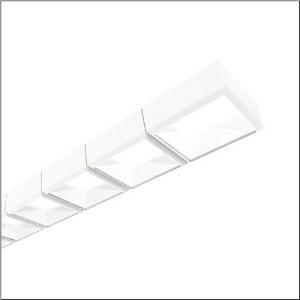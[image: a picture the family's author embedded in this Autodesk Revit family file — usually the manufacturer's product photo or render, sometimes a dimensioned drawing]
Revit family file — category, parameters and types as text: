
# Revit family: scriptus_r__11_5mz314d04wa_e059
name_source: partatom
category: Lighting Fixtures
units: mm (PartAtom-declared; Revit-internal decimal feet)

## family parameters
Cut with Voids When Loaded = No
Host = Face
Light Source = No
Part Type = Normal
Room Calculation Point = No
Round Connector Dimension = Use Diameter
Shared = No

## types (1)
- Scriptus® 11 (1 x LED 4000K / CRI = 80 (unbekannt), 3220 lm / 4820 lm, 4000K)
    Apparent Load = 120 VA
    CIE Flux Codes = - - - 0 100 / 82 95 99 100 100
    Color Rendering = 80
    Color Temperature = 4000K
    Default Elevation = 1800 mm
    Description = Scriptus® 11, office luminaire, primary optical cover: lenses, CAT 2 (L<= 3000cd/m²), light emission: direct/indirect distribution, primary light characteristic: symmetric, installation type: suspended mounting, LED, rated luminous flux: 16.060lm, luminous efficacy: 133lm/W, light colour: 840, colour temperature: 4000K, control gear: DALI, with terminal, 5-pole, mains connection: 230V, AC, 50Hz, rated input power: 120W, LED, control gear: ECG DALI, housing, luminaire housing, of aluminium, traffic white (RAL 9016), length: 3.088mm, width: 114mm, height: 57mm, protection rating (complete): IP20, insulation class (complete): insulation class I (protective earthing), certification: CE, ENEC, VDE, protection symbol: F, permissible operating ambient temperature: 0..+35°C, standard: EN 50419, packaging unit: 1 piece
    Height = 57 mm
    Lamp = 1 x LED 4000K / CRI >= 80 (unbekannt)
    Lamp Light Flux = 3220 lm / 4820 lm
    Lamp count = 1
    Length = 3088 mm
    Luminous efficacy = 134 lm/W
    Manufacturer = Siteco
    ModVariant = No
    Model = 5MZ314D04WA
    Mounting Place = Ceiling
    Mounting Type = Pendant
    Number of Poles = 1
    OnlyDefault = Yes
    Power Factor = 1
    Product Name = Scriptus® 11
    Product group = office luminaire | ceiling pendant
    ProductGroupID = 904
    Protection Class = Protection class I
    Protection Degree = IP 20
    RLX_Detail_Level = 1
    RLX_Emergency_Light_Flux = 0 lm
    RLX_Emergency_Type = 0
    RLX_Emergency_Type_DB = No
    RlxData = <blob elided: 31925 chars, md5=0f39a516>
    Socket = socket
    Standby Power = 0 W
    System Light Flux = 16080 lm
    System Power = 120 W
    Type Comments = Product without accessories
    Type Image = l_1004839.jpg
    URL = http://relux.com
    VarID = ---
    Voltage = 0 V
    Weight = 0.00 kg
    Width = 114 mm

## geometry (parser evidence)
native form markers: Blend x4, Sweep x19
no freeform markers — native parametric forms only
